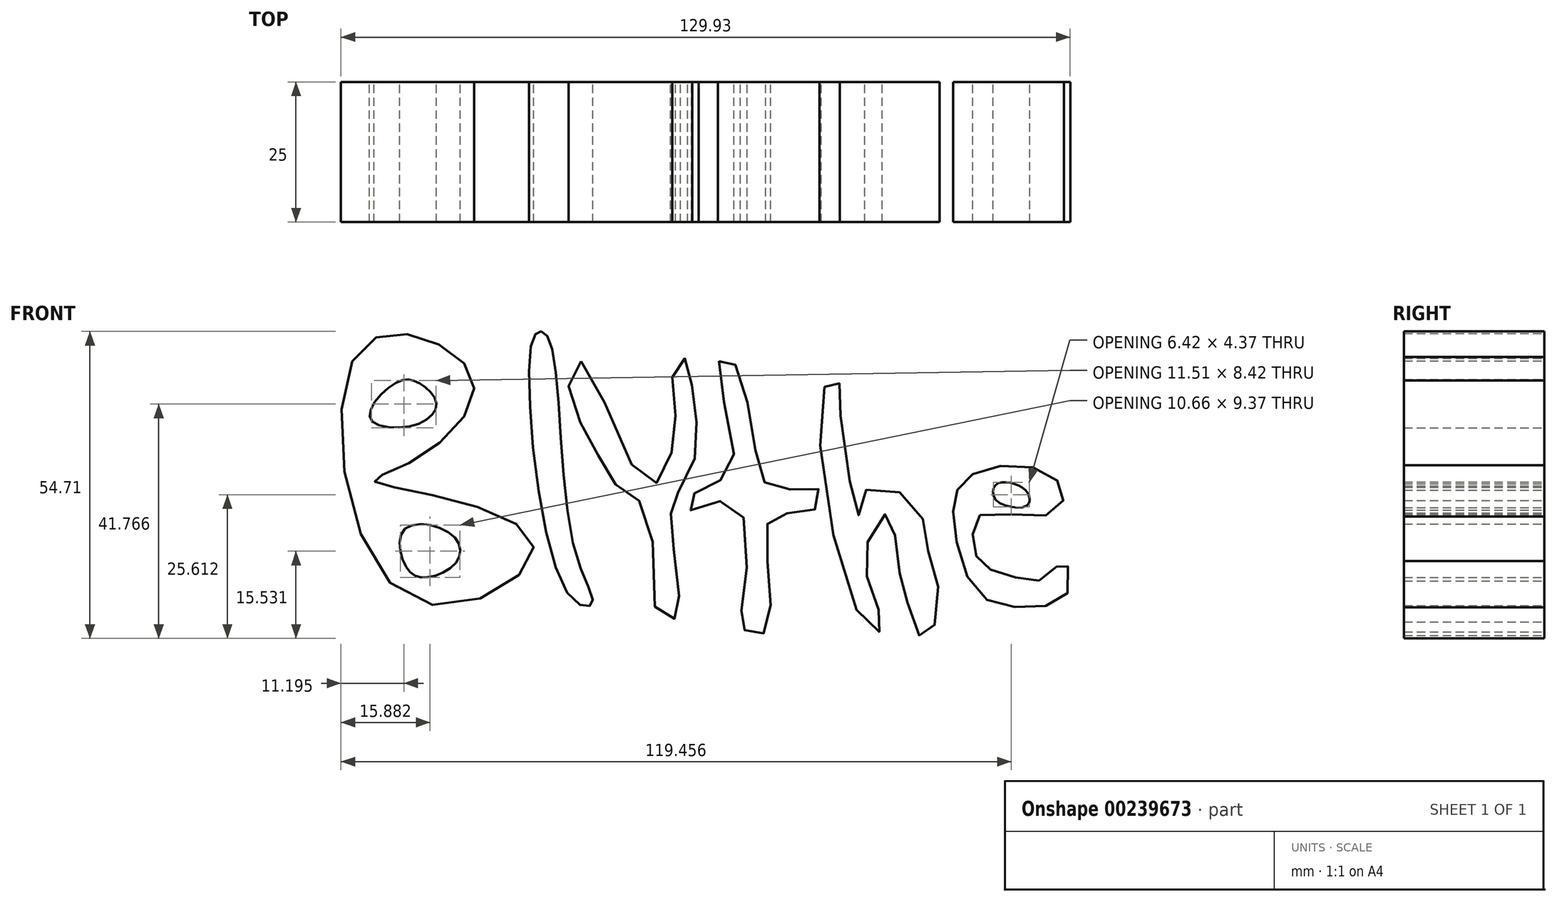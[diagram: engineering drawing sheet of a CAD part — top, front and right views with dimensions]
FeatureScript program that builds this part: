
annotation { "Feature Type Name" : "Feature", "Feature Type Description" : "" }
export const myFeature = defineFeature(function(context is Context, id is Id, definition is map)
    precondition{}
    {
        {
            var Q0;
            Q0=qCreatedBy(makeId("Front.planeOp"),FACE);
            var sketch = newSketch(context, id + "F0", { "sketchPlane" : qUnion([Q0])});
            skFitSpline(sketch, "E0", {"points": [v(-67.72, 38.56) * mm, v(-57.12, -3.86) * mm, v(-35.43, 4.82) * mm, v(-53.5, 14.7) * mm, v(-63.86, 17.35) * mm, v(-56.15, 21.2) * mm, v(-46.03, 33.98) * mm, v(-54.95, 42.66) * mm, v(-67.72, 38.56) * mm]});
            skFitSpline(sketch, "E1", {"points": [v(-35.9, 41.2) * mm, v(-29.16, -3.13) * mm, v(-25.06, -4.82) * mm, v(-28.2, 5.3) * mm, v(-32.3, 41.45) * mm, v(-34.22, 43.86) * mm, v(-35.9, 41.2) * mm]});
            skFitSpline(sketch, "E2", {"points": [v(-27, 38.56) * mm, v(-18.32, 20.73) * mm, v(-13.5, 16.87) * mm, v(-10.6, 23.62) * mm, v(-10.36, 31.57) * mm, v(-10.12, 38.56) * mm, v(-7.71, 38.56) * mm, v(-7.23, 31.57) * mm, v(-6.02, 24.1) * mm, v(-9.4, 15.66) * mm, v(-10.84, 12.53) * mm, v(-10.84, 8.2) * mm, v(-9.4, -4.1) * mm, v(-9.88, -6.99) * mm, v(-13.01, -7.47) * mm, v(-14.94, 11.57) * mm, v(-19.04, 14.94) * mm, v(-22.65, 19.52) * mm, v(-26.5, 26.5) * mm, v(-29.16, 34.7) * mm, v(-27, 38.56) * mm]});
            skFitSpline(sketch, "E3", {"points": [v(-2.4, 38.56) * mm, v(0, 19.52) * mm, v(-6.02, 15.66) * mm, v(-7.71, 12.05) * mm, v(0, 13.5) * mm, v(1.93, -3.86) * mm, v(1.93, -9.16) * mm, v(5.3, -10.12) * mm, v(6.5, 0) * mm, v(7.23, 11.09) * mm, v(14.22, 11.8) * mm, v(15.42, 15.66) * mm, v(7.71, 15.66) * mm, v(4.1, 22.41) * mm, v(0, 38.56) * mm, v(-2.4, 38.56) * mm]});
            skFitSpline(sketch, "E4", {"points": [v(16.39, 33.98) * mm, v(22.9, -7.23) * mm, v(26.5, -9.4) * mm, v(25.06, -3.13) * mm, v(23.86, 5.54) * mm, v(27.71, 11.33) * mm, v(29.4, 3.13) * mm, v(31.09, -4.1) * mm, v(33.98, -10.84) * mm, v(36.87, -4.82) * mm, v(34.7, 5.54) * mm, v(32.53, 13.01) * mm, v(23.86, 15.66) * mm, v(22.41, 11.09) * mm, v(19.04, 31.57) * mm, v(18.8, 34.94) * mm, v(16.39, 33.98) * mm]});
            skFitSpline(sketch, "E5", {"points": [v(-60, 34.7) * mm, v(-64.59, 28.44) * mm, v(-56.4, 27.23) * mm, v(-52.78, 31.09) * mm, v(-55.91, 34.7) * mm, v(-60, 34.7) * mm]});
            skFitSpline(sketch, "E6", {"points": [v(-58.32, 8.68) * mm, v(-58.32, 2.17) * mm, v(-54.7, 0) * mm, v(-48.92, 3.13) * mm, v(-50.13, 7.71) * mm, v(-58.32, 8.68) * mm]});
            skFitSpline(sketch, "E7", {"points": [v(44.1, 11.09) * mm, v(55.91, 11.09) * mm, v(59.04, 14.94) * mm, v(54.7, 19.28) * mm, v(44.1, 19.04) * mm, v(40, 15.42) * mm, v(39.52, 8.92) * mm, v(43.86, -2.9) * mm, v(52.54, -5.3) * mm, v(59.77, -2.65) * mm, v(59.04, 2.9) * mm, v(55.91, 0) * mm, v(50.37, 0) * mm, v(44.34, 2.4) * mm, v(42.9, 6.5) * mm, v(44.1, 11.09) * mm]});
            skFitSpline(sketch, "E8", {"points": [v(46.96, 13.8) * mm, v(52.43, 12.82) * mm, v(52.63, 14.97) * mm, v(50.09, 16.73) * mm, v(46.96, 16.53) * mm, v(46.96, 13.8) * mm]});
            skSolve(sketch);
        }
        {
            var Q0;
            Q0=makeQuery(id+"F0.imprint","IMPRINT",FACE,{"disambiguationData":[TD([[makeQuery(id+"F0.imprint","IMPRINT",EDGE,{"derivedFrom":sQuery(id+"F0.wireOp",EDGE,"E0")}),1.0]])]});
            var Q1;
            Q1=makeQuery(id+"F0.imprint","IMPRINT",FACE,{"disambiguationData":[TD([[makeQuery(id+"F0.imprint","IMPRINT",EDGE,{"derivedFrom":sQuery(id+"F0.wireOp",EDGE,"E1")}),1.0]])]});
            var Q2;
            Q2=makeQuery(id+"F0.imprint","IMPRINT",FACE,{"disambiguationData":[TD([[makeQuery(id+"F0.imprint","IMPRINT",EDGE,{"derivedFrom":sQuery(id+"F0.wireOp",EDGE,"E2")}),-1.0]])]});
            var Q3;
            Q3=makeQuery(id+"F0.imprint","IMPRINT",FACE,{"disambiguationData":[TD([[makeQuery(id+"F0.imprint","IMPRINT",EDGE,{"derivedFrom":sQuery(id+"F0.wireOp",EDGE,"E3")}),1.0]])]});
            var Q4;
            Q4=makeQuery(id+"F0.imprint","IMPRINT",FACE,{"disambiguationData":[TD([[makeQuery(id+"F0.imprint","IMPRINT",EDGE,{"derivedFrom":sQuery(id+"F0.wireOp",EDGE,"E4")}),1.0]])]});
            var Q5;
            Q5=makeQuery(id+"F0.imprint","IMPRINT",FACE,{"disambiguationData":[TD([[makeQuery(id+"F0.imprint","IMPRINT",EDGE,{"derivedFrom":sQuery(id+"F0.wireOp",EDGE,"E7")}),1.0]])]});
            extrude(context, id + "F1", {"entities" : qUnion([Q0, Q1, Q2, Q3, Q4, Q5]), "depth" : 25 * mm});
        }
    });
